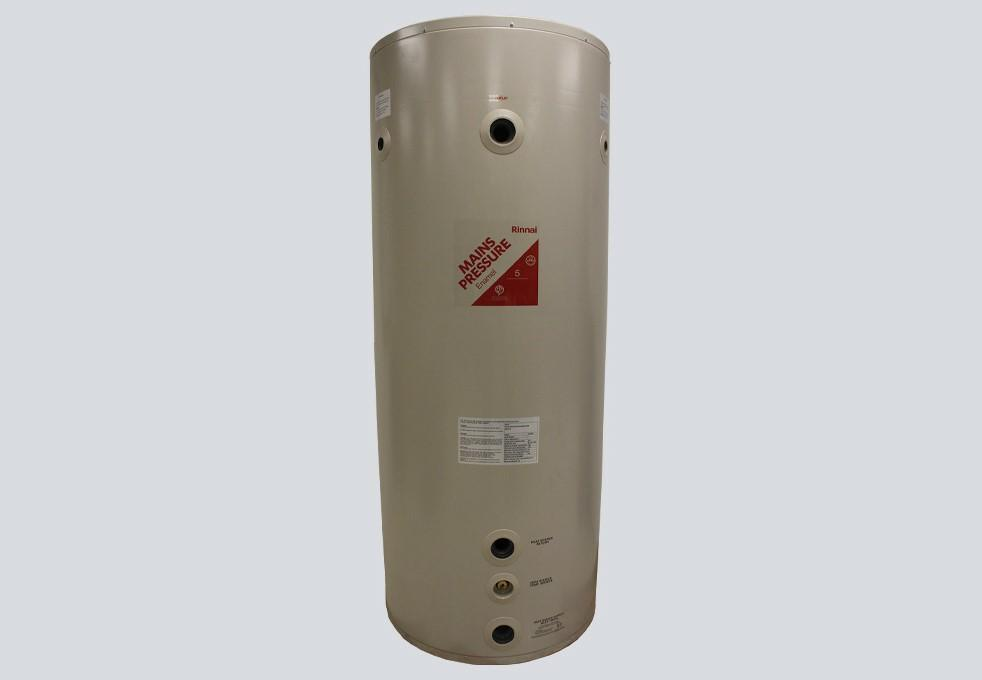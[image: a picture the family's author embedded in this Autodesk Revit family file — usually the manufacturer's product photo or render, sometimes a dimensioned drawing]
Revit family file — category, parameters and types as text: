
# Revit family: MEC0450720E
name_source: partatom
category: Generic Models
revit_build: Autodesk Revit 2018 (Build: 20190510_1515(x64)
units: mm (PartAtom-declared; Revit-internal decimal feet)

## family parameters
Can host rebar = No
Cut with Voids When Loaded = No
Host = Face
Part Type = Normal
Room Calculation Point = No
Round Connector Dimension = Use Diameter
Shared = No

## types (1)
- MEC0450720E
    Anodes = 2 x 25mm
    Capacity = 450L
    Cold Inlet = 108 mm
    Cold Inlet Connection (Inner) = 1 1/2"
    Cold Inlet Connection (Outer) = 2"
    Cold water Pressure Relief Valve (not supplied) = 850 kPa (approx.)
    Construction = Coloursteel outer (dune), enamel steel inner
    Controlled heating source outlet temp. = Below 76°C
    Default Elevation = 1219 mm
    Description = 450L Commercial Cylinder
    Hot Outlet = 1370 mm  [stored 4.49475 ft]
    Hot Outlet Connection (Inner) = 1 1/2"
    Hot Outlet Connection (Outer) = 2"
    Hot Return Connection (Inner) = 1 1/2"
    Hot Return Connection (Outer) = 2"
    Hot Water Return = 127 mm
    Ingress protection (IP) rating = IPX4
    Inner Cylinder Height = 1700 mm
    Inner Cylinder Radius = 309 mm
    Insulation = 51mm of polyeurethane-injected foam
    Outer Cylinder Height = 1763 mm
    Outer Cylinder Radius = 360 mm  [stored 1.1811 ft]
    Pressure Limiting valve (not supplied) = 700 kPa (approx.)
    Rinnai Part No. = MEC0450720E
    Sensor = Thermowell fitted suitable for max. 6.5mm temperature probe
    Sensor Port = 146 mm  [stored 0.479003 ft]
    Sensor Port Connection = 3/4"
    TPR = 1370 mm  [stored 4.49475 ft]
    TPR Angle = 59.75°
    TPR Connection = 1"
    TPR ports = 25 mm (1 inch)  BSP female ports on side of cylinder
    TPR valve pressure rating = 1000 kPa
    Type Comments = The manufacturer reserves the right for product design changes without notice
    Type Image = 450l-sacon-cylinder-website.jpg
    Warranty = Parts and labour 1 year, Inner cylinder 5 years
    Weight empty/full = 125.5kg / 579.5kg

note: [stored X ft] marks values corroborated as IEEE doubles in the binary element streams (Revit-internal decimal feet)

## geometry (parser evidence)
native form markers: Sweep x3
no freeform markers — native parametric forms only
